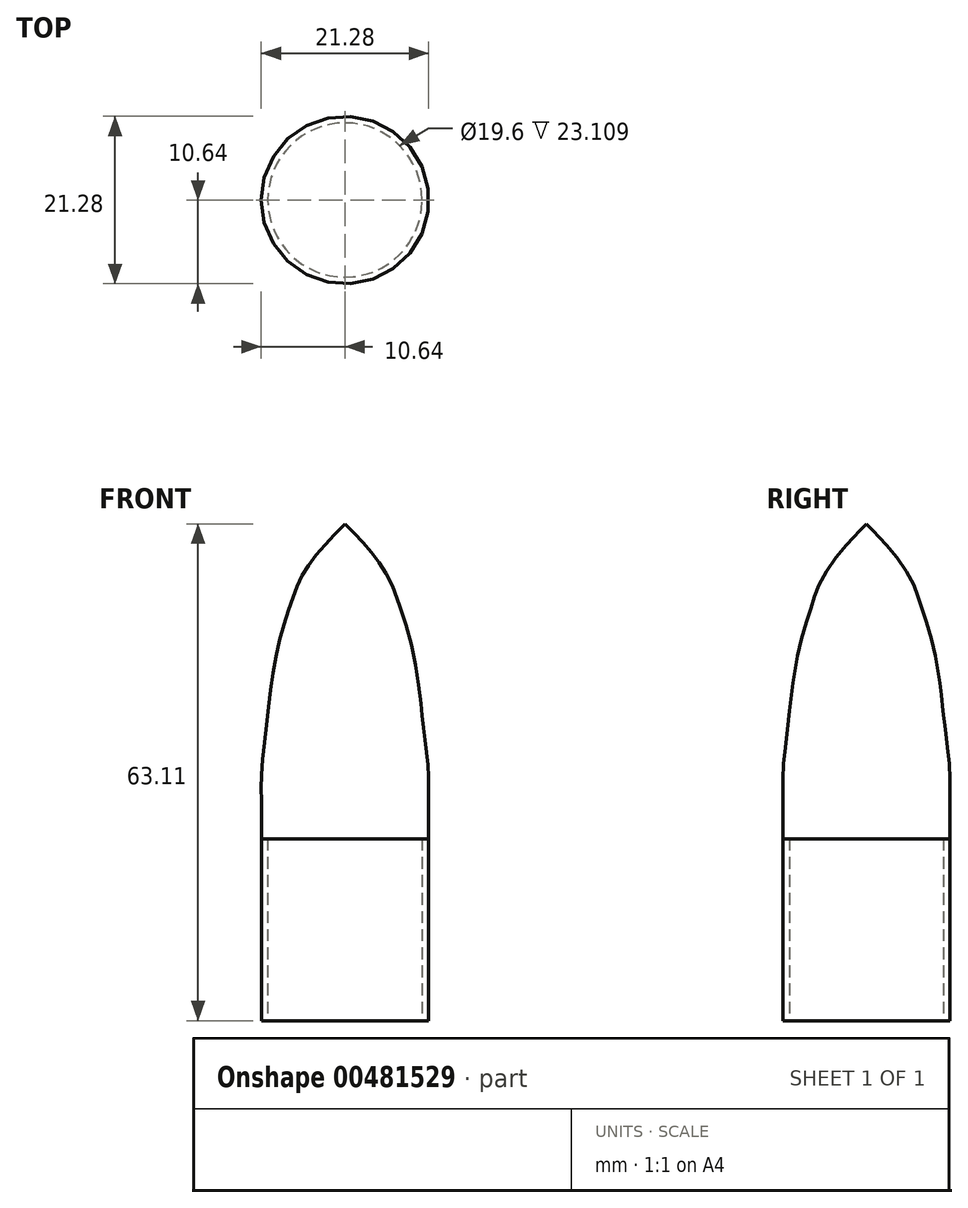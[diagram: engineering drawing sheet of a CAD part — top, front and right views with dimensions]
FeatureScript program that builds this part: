
annotation { "Feature Type Name" : "Feature", "Feature Type Description" : "" }
export const myFeature = defineFeature(function(context is Context, id is Id, definition is map)
    precondition{}
    {
        {
            var Q0;
            Q0=qCreatedBy(makeId("Front.planeOp"),FACE);
            var sketch = newSketch(context, id + "F0", { "sketchPlane" : qUnion([Q0])});
            skLineSegment(sketch, "E0", {"start": v(-9.8, 0) * mm, "end": v(-10.6, 0) * mm});
            skLineSegment(sketch, "E1", {"start": v(-10.6, 0) * mm, "end": v(-10.6, 23.1) * mm});
            skLineSegment(sketch, "E2", {"start": v(-9.8, 23.1) * mm, "end": v(-9.8, 0) * mm});
            skLineSegment(sketch, "E3", {"start": v(-9.8, 23.1) * mm, "end": v(0, 23.1) * mm});
            skLineSegment(sketch, "E4", {"start": v(0, 23.1) * mm, "end": v(0, 63.1) * mm});
            skFitSpline(sketch, "E5", {"points": [v(-10.6, 23.1) * mm, v(-10.6, 27.3) * mm, v(-10.6, 31.5) * mm, v(-9.8, 38.88) * mm, v(-8.77, 46.26) * mm, v(-7.03, 52.5) * mm, v(-5.66, 56.08) * mm, v(-3.5, 59.33) * mm, v(0, 63.1) * mm], "startDerivative": vector(0.27, 39.44) * mm, "endDerivative": vector(31.3, 31.85) * mm});
            skLineSegment(sketch, "E6", {"start": v(0, 0) * mm, "end": v(0, 67.83) * mm});
            skSolve(sketch);
        }
        {
            var Q0;
            Q0=makeQuery(id+"F0.imprint","IMPRINT",FACE,{"disambiguationData":[TD([[makeQuery(id+"F0.imprint","IMPRINT",EDGE,{"derivedFrom":sQuery(id+"F0.wireOp",EDGE,"E0")}),-1.0]])]});
            var Q1;
            Q1=sQuery(id+"F0.wireOp",EDGE,"E6");
            revolve(context, id + "F1", {"entities" : qUnion([Q0]), "axis" : qUnion([Q1]), "revolveType" : RevolveType.FULL});
        }
    });
